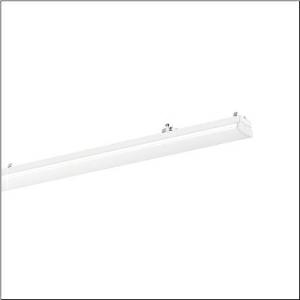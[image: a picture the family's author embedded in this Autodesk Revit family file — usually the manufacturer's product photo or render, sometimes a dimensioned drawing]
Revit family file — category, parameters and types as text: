
# Revit family: licross_11_recessed_opal_mo_51te1ddn46xg
name_source: partatom
category: Lighting Fixtures
units: mm (PartAtom-declared; Revit-internal decimal feet)

## family parameters
Cut with Voids When Loaded = No
Host = Face
Light Source = No
Part Type = Normal
Room Calculation Point = No
Round Connector Dimension = Use Diameter
Shared = No

## types (1)
- --- (1 x LED, 6320 lm, 35.2 W, 4000K)
    Apparent Load = 35 VA
    CIE Flux Codes = 44 73 91 87 100
    Color Rendering = 80
    Color Temperature = 4000K
    Default Elevation = 1800 mm
    Description = Licross 11 recessed opal MO, luminaire insert, of sheet steel, coil coated, white, length: 1.500mm, width: 76mm, height: 87mm, LED rated luminous flux: 6.320lm, light colour: 840, SDCM (Standard Deviation of Colour Matching)MacAdam ≤ 2 SDCM (initial), control gear: DALI 2, with plug, 5-pole, with phase selection, mains connection: 220..240V, AC, 50/60Hz, rated input power: 35W, internal wiring halogen-free, primary optical cover: cover, of PMMA, light emission: direct with ceiling illumination distribution, primary light characteristic: symmetric, protection rating (complete): IP54, insulation class (complete): insulation class I (protective earthing), certification: CE, ENEC, VDE, UKCA, protection symbol: D if used in an environment with non-conductive dust loads with corresponding accessories, impact resistance: IK06, permissible ambient temperature for indoor applications: -25..+40°C, corresponds to IFS (International Featured Standards) requirements for safety and quality in the food industry, reducing of maximum allowable ambient temperature of 5°C with ceiling mounting, LABS conformity tested according to VDMA 24364:2018-05, The light source and the operating device comply with the requirements of the Ecodesign Regulation (EU) 2019/2020 and are replaceable in accordance with this regulation, packaging unit: 1 piece
    Height = 83 mm
    Lamp = 1 x LED
    Lamp Light Flux = 6320 lm
    Lamp Power = 35.2 W
    Lamp count = 1
    Length = 1500 mm
    Luminous efficacy = 180 lm/W
    Manufacturer = Siteco
    ModVariant = No
    Model = 51TE1DDN46XG
    Mounting Place = Ceiling
    Mounting Type = Pendant
    Number of Poles = 1
    OnlyDefault = Yes
    Power Factor = 1
    Product Name = Licross 11 recessed opal MO
    Product group = luminaire insert | ceiling pendant
    ProductGroupID = 901
    Protection Class = Protection class I
    Protection Degree = IP 54
    RLX_Detail_Level = 1
    RLX_Emergency_Light_Flux = 0 lm
    RLX_Emergency_Type = 0
    RLX_Emergency_Type_DB = No
    RlxData = <blob elided: 26909 chars, md5=335d26b0>
    Socket = socket
    Standby Power = 0 W
    System Light Flux = 6320 lm
    System Power = 35 W
    Type Comments = factory setting: luminous flux: 100 % | dim-lin: 254 | 238 mA
    Type Image = l_1313666.jpg
    URL = http://relux.com
    VarID = @adj_083729
    Voltage = 0 V
    Weight = 0.00 kg
    Width = 76 mm

## geometry (parser evidence)
native form markers: Blend x4, Sweep x14
no freeform markers — native parametric forms only
